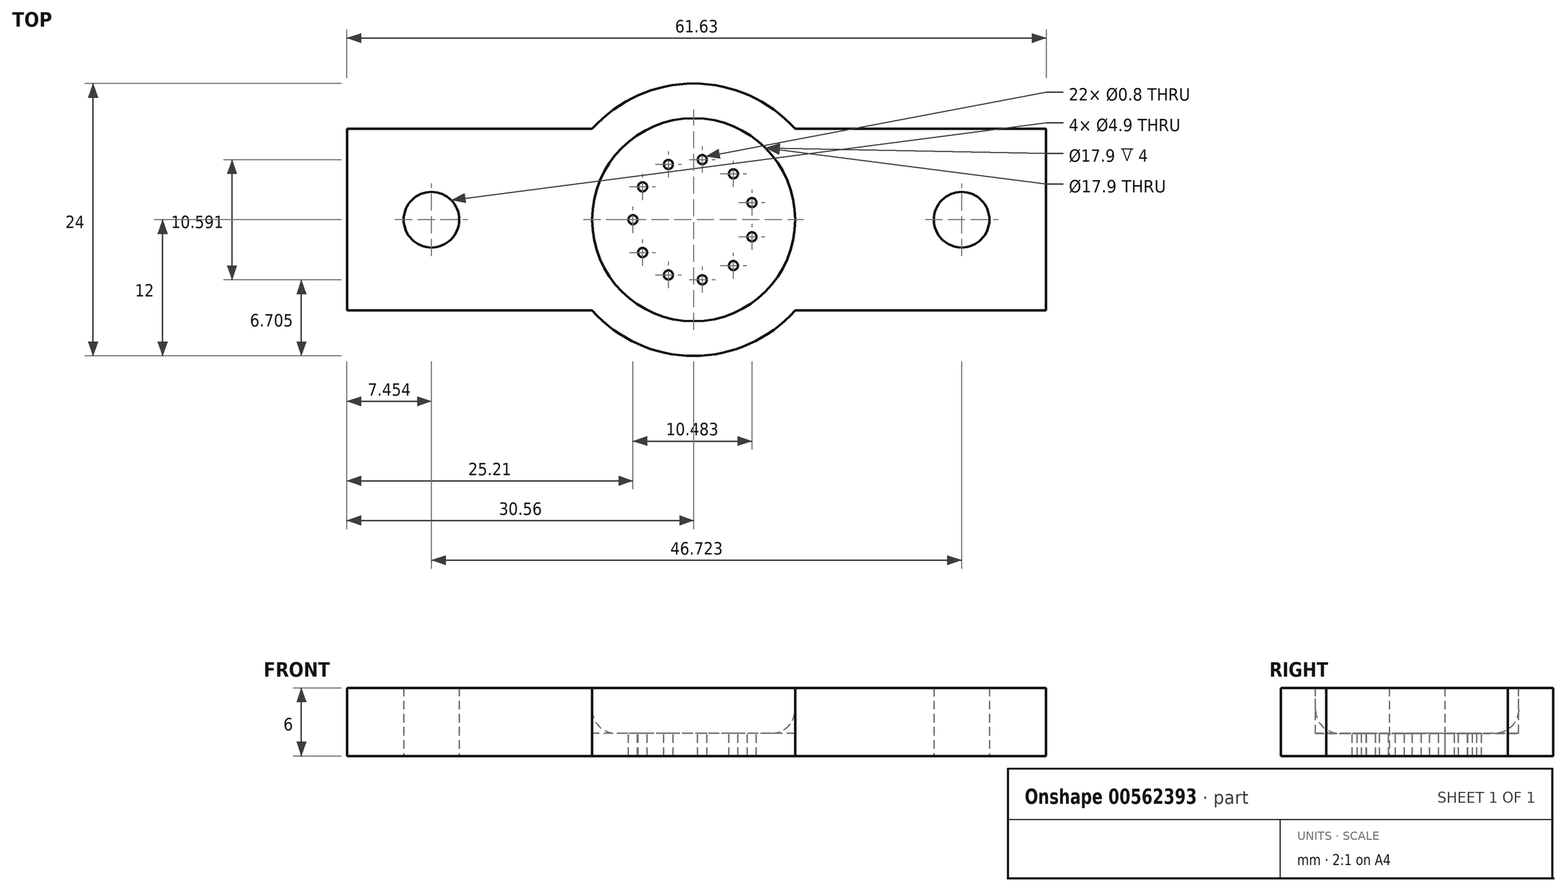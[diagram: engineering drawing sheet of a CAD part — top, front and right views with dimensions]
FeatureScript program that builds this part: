
annotation { "Feature Type Name" : "Feature", "Feature Type Description" : "" }
export const myFeature = defineFeature(function(context is Context, id is Id, definition is map)
    precondition{}
    {
        {
            var Q0;
            Q0=qCreatedBy(makeId("Top.planeOp"),FACE);
            var sketch = newSketch(context, id + "F0", { "sketchPlane" : qUnion([Q0])});
            skCircle(sketch, "E0", {"center": v(0, 0) * mm, "radius": 12 * mm});
            skLineSegment(sketch, "E1", {"start": v(8.94, 8) * mm, "end": v(31.07, 8) * mm});
            skLineSegment(sketch, "E2", {"start": v(31.07, 8) * mm, "end": v(31.07, -8) * mm});
            skLineSegment(sketch, "E3", {"start": v(31.07, -8) * mm, "end": v(8.94, -8) * mm});
            skCircle(sketch, "E4", {"center": v(23.62, 0) * mm, "radius": 2.45 * mm});
            skLineSegment(sketch, "E5", {"start": v(-8.94, -8) * mm, "end": v(-30.56, -8) * mm});
            skLineSegment(sketch, "E6", {"start": v(-30.56, -8) * mm, "end": v(-30.56, 8) * mm});
            skLineSegment(sketch, "E7", {"start": v(-30.56, 8) * mm, "end": v(-8.94, 8) * mm});
            skCircle(sketch, "E8", {"center": v(-23.1, 0) * mm, "radius": 2.45 * mm});
            skSolve(sketch);
        }
        {
            var Q0;
            Q0 = qSketchRegion(id + "F0", true);
            extrude(context, id + "F1", {"entities" : qUnion([Q0]), "depth" : 6 * mm, "offsetDistance" : 25 * mm});
        }
        {
            var Q0;
            Q0=makeQuery(id+"F1.opExtrude","CAP_FACE",FACE,{"disambiguationData":[OSD([sQuery(id+"F0.wireOp",EDGE,"E0"),sQuery(id+"F0.wireOp",EDGE,"E1"),sQuery(id+"F0.wireOp",EDGE,"E2"),sQuery(id+"F0.wireOp",EDGE,"E3"),sQuery(id+"F0.wireOp",EDGE,"E4"),sQuery(id+"F0.wireOp",EDGE,"E5"),sQuery(id+"F0.wireOp",EDGE,"E6"),sQuery(id+"F0.wireOp",EDGE,"E7"),sQuery(id+"F0.wireOp",EDGE,"E8")])],"isStart":false});
            var sketch = newSketch(context, id + "F2", { "sketchPlane" : qUnion([Q0])});
            skCircle(sketch, "E9", {"center": v(0, 0) * mm, "radius": 8.95 * mm});
            skSolve(sketch);
        }
        {
            var Q0;
            Q0=makeQuery(id+"F2.imprint","IMPRINT",FACE,{"disambiguationData":[TD([[makeQuery(id+"F2.imprint","IMPRINT",EDGE,{"derivedFrom":sQuery(id+"F2.wireOp",EDGE,"E9")}),1.0]])]});
            extrude(context, id + "F3", {"entities" : qUnion([Q0]), "operationType" : NewBodyOperationType.REMOVE, "oppositeDirection" : true, "depth" : 4 * mm, "offsetDistance" : 25 * mm});
        }
        {
            var Q0;
            Q0=makeQuery(id+"F3.boolean.opBoolean","COPY",FACE,{"derivedFrom":makeQuery(id+"F3.opExtrude","CAP_FACE",FACE,{"disambiguationData":[OSD([sQuery(id+"F2.wireOp",EDGE,"E9")])],"isStart":false})});
            fillet(context, id + "F4", {"entities" : qUnion([Q0]), "radius" : 2.1 * mm, "tangentPropagation" : true, "allowEdgeOverflow" : false});
        }
        {
            var Q0;
            Q0=makeQuery(id+"F3.boolean.opBoolean","COPY",FACE,{"derivedFrom":makeQuery(id+"F3.opExtrude","CAP_FACE",FACE,{"disambiguationData":[OSD([sQuery(id+"F2.wireOp",EDGE,"E9")])],"isStart":false})});
            var sketch = newSketch(context, id + "F5", { "sketchPlane" : qUnion([Q0])});
            skCircle(sketch, "E10", {"center": v(-5.35, 0) * mm, "radius": 0.4 * mm});
            skCircle(sketch, "E11.1.0", {"center": v(-4.5, -2.9) * mm, "radius": 0.4 * mm});
            skCircle(sketch, "E11.2.0", {"center": v(-2.22, -4.87) * mm, "radius": 0.4 * mm});
            skCircle(sketch, "E11.3.0", {"center": v(0.76, -5.3) * mm, "radius": 0.4 * mm});
            skCircle(sketch, "E11.4.0", {"center": v(3.5, -4.04) * mm, "radius": 0.4 * mm});
            skCircle(sketch, "E11.5.0", {"center": v(5.13, -1.5) * mm, "radius": 0.4 * mm});
            skCircle(sketch, "E11.6.0", {"center": v(5.13, 1.5) * mm, "radius": 0.4 * mm});
            skCircle(sketch, "E11.7.0", {"center": v(3.5, 4.04) * mm, "radius": 0.4 * mm});
            skCircle(sketch, "E11.8.0", {"center": v(0.76, 5.3) * mm, "radius": 0.4 * mm});
            skCircle(sketch, "E11.9.0", {"center": v(-2.22, 4.87) * mm, "radius": 0.4 * mm});
            skCircle(sketch, "E11.10.0", {"center": v(-4.5, 2.9) * mm, "radius": 0.4 * mm});
            skPoint(sketch, "E11.center", {"position": v(0, 0) * mm});
            skSolve(sketch);
        }
        {
            var Q0;
            Q0 = qSketchRegion(id + "F5", true);
            extrude(context, id + "F6", {"entities" : qUnion([Q0]), "operationType" : NewBodyOperationType.REMOVE, "endBound" : BoundingType.THROUGH_ALL, "oppositeDirection" : true, "depth" : 25 * mm, "offsetDistance" : 25 * mm});
        }
    });
